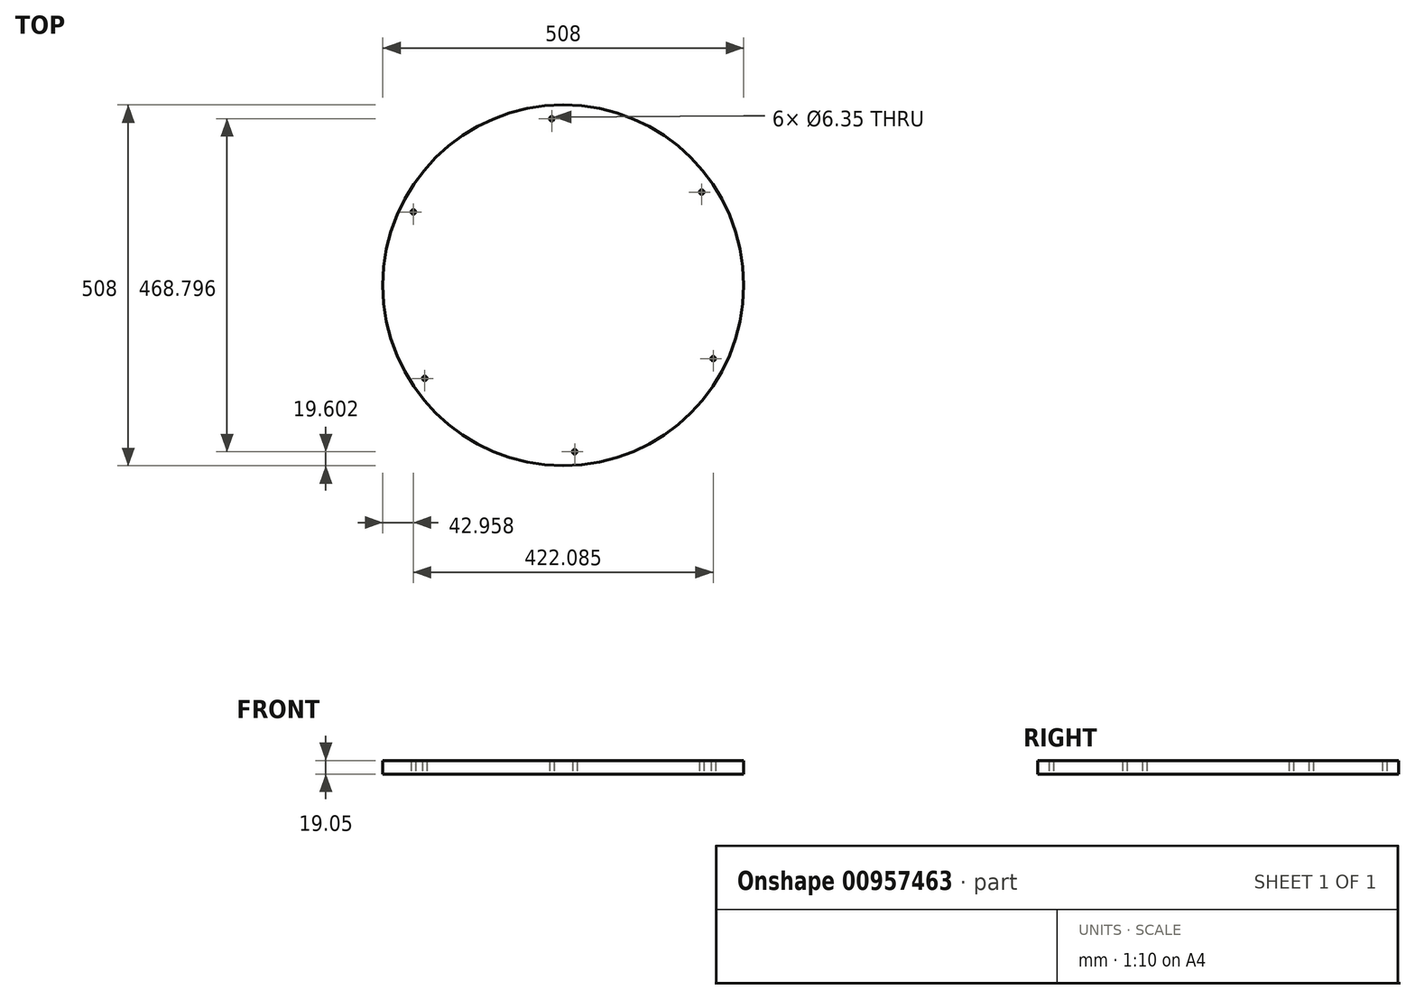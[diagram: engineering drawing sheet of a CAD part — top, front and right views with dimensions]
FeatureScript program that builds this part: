
annotation { "Feature Type Name" : "Feature", "Feature Type Description" : "" }
export const myFeature = defineFeature(function(context is Context, id is Id, definition is map)
    precondition{}
    {
        {
            var Q0;
            Q0=qCreatedBy(makeId("Top.planeOp"),FACE);
            var sketch = newSketch(context, id + "F0", { "sketchPlane" : qUnion([Q0])});
            skCircle(sketch, "E0", {"center": v(0, 0) * mm, "radius": 254 * mm});
            skCircle(sketch, "E1", {"center": v(0, 0) * mm, "radius": 234.95 * mm});
            skCircle(sketch, "E2", {"center": v(-211.04, 103.26) * mm, "radius": 3.18 * mm});
            skCircle(sketch, "E3.1.0", {"center": v(-194.95, -131.14) * mm, "radius": 3.18 * mm});
            skCircle(sketch, "E3.2.0", {"center": v(16.1, -234.4) * mm, "radius": 3.18 * mm});
            skCircle(sketch, "E4.1.3.0", {"center": v(211.04, -103.26) * mm, "radius": 3.18 * mm});
            skCircle(sketch, "E4.1.4.0", {"center": v(194.95, 131.14) * mm, "radius": 3.18 * mm});
            skCircle(sketch, "E4.1.5.0", {"center": v(-16.1, 234.4) * mm, "radius": 3.18 * mm});
            skSolve(sketch);
        }
        {
            var Q0;
            {var subQ0=sQuery(id+"F0.wireOp",EDGE,"E1");var subQ1=sQuery(id+"F0.wireOp",EDGE,"E2");var subQ5=makeQuery(id+"F0.imprint","INTERSECT",VERTEX,{"disambiguationData":[OD(0.0)],"derivedFrom":[subQ1,subQ0]});Q0=makeQuery(id+"F0.imprint","IMPRINT",FACE,{"disambiguationData":[TD([[makeQuery(id+"F0.imprint","IMPRINT",EDGE,{"disambiguationData":[TD([[subQ5,1.0]])],"derivedFrom":subQ1}),-1.0]])]});}
            var Q1;
            Q1=makeQuery(id+"F0.imprint","IMPRINT",FACE,{"disambiguationData":[TD([[makeQuery(id+"F0.imprint","IMPRINT",EDGE,{"derivedFrom":sQuery(id+"F0.wireOp",EDGE,"E0")}),1.0]])]});
            extrude(context, id + "F1", {"entities" : qUnion([Q0, Q1]), "depth" : 19.05 * mm, "offsetDistance" : 25.4 * mm});
        }
    });
